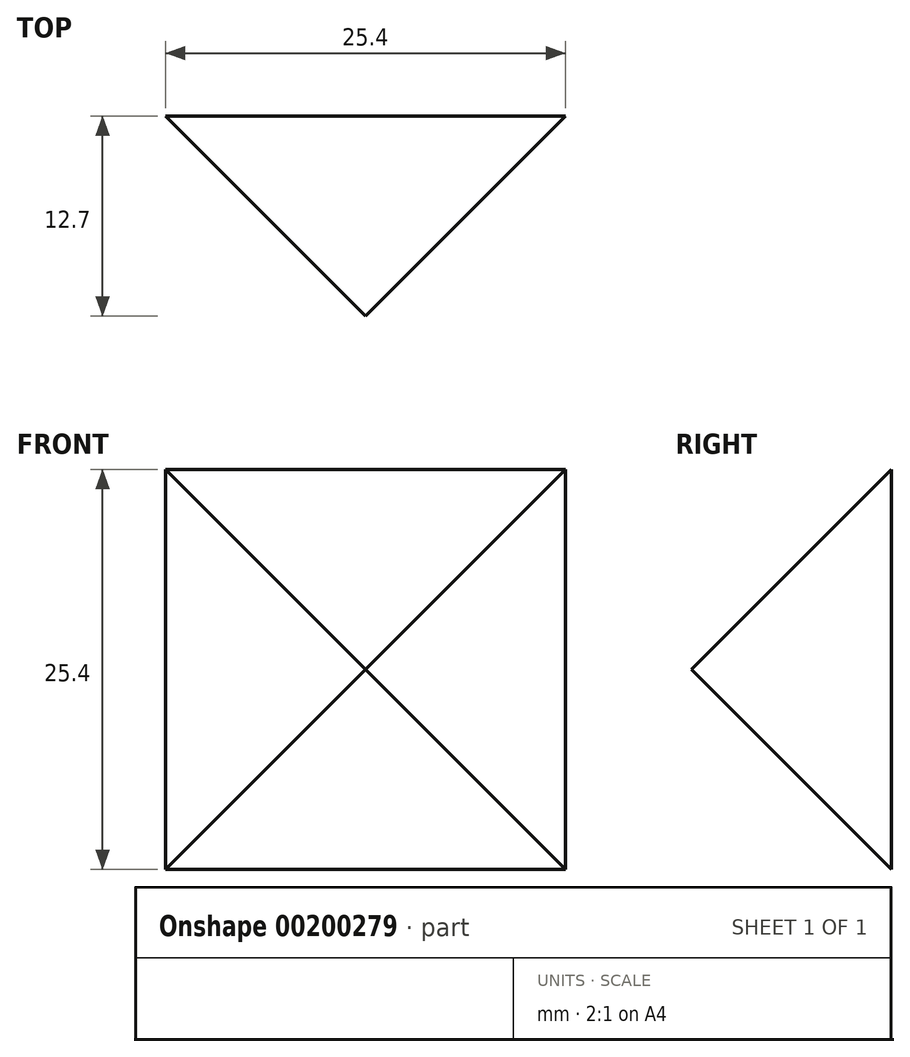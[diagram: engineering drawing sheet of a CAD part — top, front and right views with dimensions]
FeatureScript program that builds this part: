
annotation { "Feature Type Name" : "Feature", "Feature Type Description" : "" }
export const myFeature = defineFeature(function(context is Context, id is Id, definition is map)
    precondition{}
    {
        {
            var Q0;
            Q0=qCreatedBy(makeId("Front.planeOp"),FACE);
            var sketch = newSketch(context, id + "F0", { "sketchPlane" : qUnion([Q0])});
            skLineSegment(sketch, "E0.bottom", {"start": v(-12472.22, 4165.04) * mm, "end": v(-12446.82, 4165.04) * mm});
            skLineSegment(sketch, "E0.top", {"start": v(-12472.22, 4139.64) * mm, "end": v(-12446.82, 4139.64) * mm});
            skLineSegment(sketch, "E0.left", {"start": v(-12472.22, 4165.04) * mm, "end": v(-12472.22, 4139.64) * mm});
            skLineSegment(sketch, "E0.right", {"start": v(-12446.82, 4165.04) * mm, "end": v(-12446.82, 4139.64) * mm});
            skSolve(sketch);
        }
        {
            var Q0;
            Q0 = qSketchRegion(id + "F0", true);
            extrude(context, id + "F1", {"entities" : qUnion([Q0]), "depth" : 25.4 * mm});
        }
        {
            var Q0;
            Q0=makeQuery(id+"F1.opExtrude","CAP_EDGE",EDGE,{"disambiguationData":[OSD([sQuery(id+"F0.wireOp",EDGE,"E0.right")])],"isStart":false});
            var Q1;
            Q1=makeQuery(id+"F1.opExtrude","CAP_EDGE",EDGE,{"disambiguationData":[OSD([sQuery(id+"F0.wireOp",EDGE,"E0.top")])],"isStart":false});
            var Q2;
            Q2=makeQuery(id+"F1.opExtrude","CAP_EDGE",EDGE,{"disambiguationData":[OSD([sQuery(id+"F0.wireOp",EDGE,"E0.left")])],"isStart":false});
            var Q3;
            Q3=makeQuery(id+"F1.opExtrude","CAP_EDGE",EDGE,{"disambiguationData":[OSD([sQuery(id+"F0.wireOp",EDGE,"E0.bottom")])],"isStart":false});
            chamfer(context, id + "F2", {"entities" : qUnion([Q0, Q1, Q2, Q3]), "width" : 12.7 * mm, "tangentPropagation" : true});
        }
        {
            var Q0;
            Q0=makeQuery(id+"F1.opExtrude","SWEPT_FACE",FACE,{"disambiguationData":[OSD([sQuery(id+"F0.wireOp",EDGE,"E0.top")])]});
            var sketch = newSketch(context, id + "F3", { "sketchPlane" : qUnion([Q0])});
            skLineSegment(sketch, "E1.bottom", {"start": v(-12472.22, 12.7) * mm, "end": v(-12446.82, 12.7) * mm});
            skLineSegment(sketch, "E1.top", {"start": v(-12472.22, 0) * mm, "end": v(-12446.82, 0) * mm});
            skLineSegment(sketch, "E1.left", {"start": v(-12472.22, 12.7) * mm, "end": v(-12472.22, 0) * mm});
            skLineSegment(sketch, "E1.right", {"start": v(-12446.82, 12.7) * mm, "end": v(-12446.82, 0) * mm});
            skSolve(sketch);
        }
        {
            var Q0;
            Q0 = qSketchRegion(id + "F3", true);
            extrude(context, id + "F4", {"entities" : qUnion([Q0]), "operationType" : NewBodyOperationType.REMOVE, "oppositeDirection" : true, "depth" : 25.4 * mm});
        }
    });
